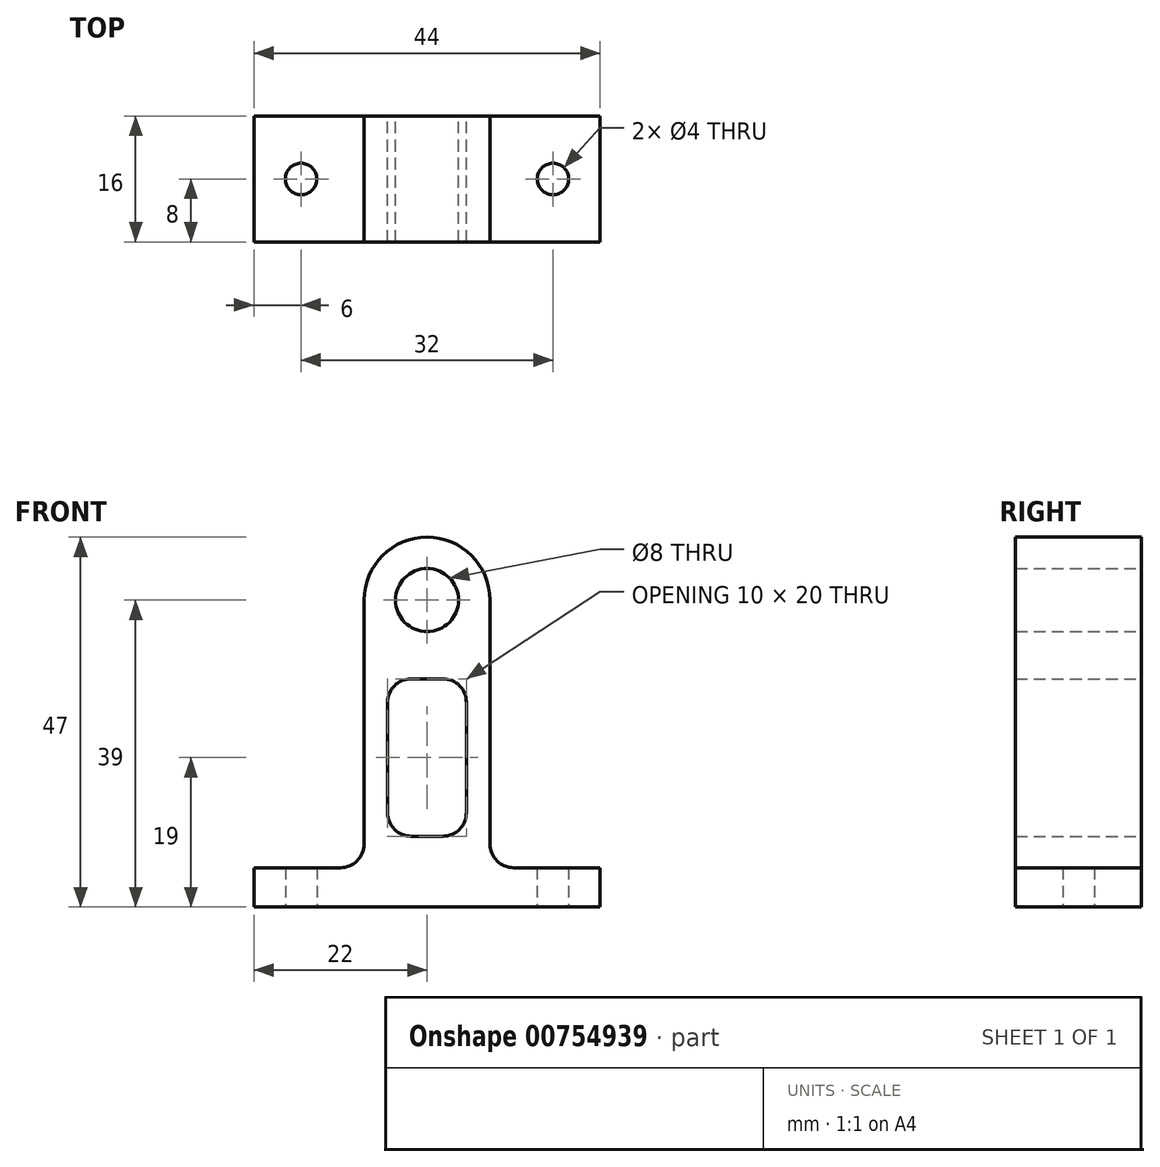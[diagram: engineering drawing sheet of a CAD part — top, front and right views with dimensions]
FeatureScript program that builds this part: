
annotation { "Feature Type Name" : "Feature", "Feature Type Description" : "" }
export const myFeature = defineFeature(function(context is Context, id is Id, definition is map)
    precondition{}
    {
        {
            var Q0;
            Q0=qCreatedBy(makeId("Front.planeOp"),FACE);
            var sketch = newSketch(context, id + "F0", { "sketchPlane" : qUnion([Q0])});
            skLineSegment(sketch, "E0.bottom", {"start": v(-22, 2.5) * mm, "end": v(-8, 2.5) * mm});
            skLineSegment(sketch, "E0.top", {"start": v(-22, -2.5) * mm, "end": v(22, -2.5) * mm});
            skLineSegment(sketch, "E0.left", {"start": v(-22, 2.5) * mm, "end": v(-22, -2.5) * mm});
            skLineSegment(sketch, "E0.right", {"start": v(22, 2.5) * mm, "end": v(22, -2.5) * mm});
            skPoint(sketch, "E0.middle", {"position": v(0, 0) * mm});
            skPoint(sketch, "E1", {"position": v(0, 36.5) * mm});
            skArc(sketch, "E2", {"start": v(8, 36.5) * mm, "mid": v(0, 44.5) * mm, "end": v(-8, 36.5) * mm});
            skLineSegment(sketch, "E3", {"start": v(8, 36.5) * mm, "end": v(8, 2.5) * mm});
            skLineSegment(sketch, "E4.0", {"start": v(-8, 36.5) * mm, "end": v(-8, 2.5) * mm});
            skLineSegment(sketch, "E5.trimOffspring", {"start": v(8, 2.5) * mm, "end": v(22, 2.5) * mm});
            skLineSegment(sketch, "E6.0", {"start": v(5, 26.5) * mm, "end": v(5, 6.5) * mm});
            skLineSegment(sketch, "E7.0", {"start": v(-5, 26.5) * mm, "end": v(-5, 6.5) * mm});
            skLineSegment(sketch, "E8.0", {"start": v(-5, 6.5) * mm, "end": v(5, 6.5) * mm});
            skLineSegment(sketch, "E9.0", {"start": v(-5, 26.5) * mm, "end": v(5, 26.5) * mm});
            skSolve(sketch);
        }
        {
            var Q0;
            Q0=makeQuery(id+"F0.imprint","IMPRINT",FACE,{"disambiguationData":[TD([[makeQuery(id+"F0.imprint","IMPRINT",EDGE,{"derivedFrom":sQuery(id+"F0.wireOp",EDGE,"E0.bottom")}),-1.0]])]});
            extrude(context, id + "F1", {"entities" : qUnion([Q0]), "depth" : 16 * mm, "offsetDistance" : 25 * mm});
        }
        {
            var Q0;
            Q0=sQuery(id+"F0.wireOp",VERTEX,"E1");
            var Q1;
            Q1=makeQuery(id+"F1.opExtrude","SWEPT_BODY",BODY,{"disambiguationData":[OSD([sQuery(id+"F0.wireOp",EDGE,"E0.bottom"),sQuery(id+"F0.wireOp",EDGE,"E0.top"),sQuery(id+"F0.wireOp",EDGE,"E0.left"),sQuery(id+"F0.wireOp",EDGE,"E0.right"),sQuery(id+"F0.wireOp",EDGE,"E2"),sQuery(id+"F0.wireOp",EDGE,"E3"),sQuery(id+"F0.wireOp",EDGE,"E4.0"),sQuery(id+"F0.wireOp",EDGE,"E5.trimOffspring")])]});
            hole(context, id + "F2", {"style" : HoleStyle.SIMPLE, "endStyle" : HoleEndStyle.THROUGH, "oppositeDirection" : true, "holeDiameter" : 8 * mm, "majorDiameter" : 5 * mm, "isTappedThrough" : true, "tappedDepth" : 8 * mm, "tapClearance" : 3, "locations" : qUnion([Q0]), "scope" : qUnion([Q1])});
        }
        {
            var Q0;
            Q0=makeQuery(id+"F1.opExtrude","SWEPT_FACE",FACE,{"disambiguationData":[OSD([sQuery(id+"F0.wireOp",EDGE,"E0.top")])]});
            var sketch = newSketch(context, id + "F3", { "sketchPlane" : qUnion([Q0])});
            skLineSegment(sketch, "E10.bottom", {"start": v(-22, 0) * mm, "end": v(22, 0) * mm});
            skLineSegment(sketch, "E10.top", {"start": v(-22, 16) * mm, "end": v(22, 16) * mm});
            skLineSegment(sketch, "E10.left", {"start": v(-22, 0) * mm, "end": v(-22, 16) * mm});
            skLineSegment(sketch, "E10.right", {"start": v(22, 0) * mm, "end": v(22, 16) * mm});
            skLineSegment(sketch, "E11.0", {"start": v(-16, 0) * mm, "end": v(-16, 16) * mm});
            skLineSegment(sketch, "E12.0", {"start": v(16, 0) * mm, "end": v(16, 16) * mm});
            skLineSegment(sketch, "E13.0", {"start": v(-18, 8) * mm, "end": v(22, 8) * mm});
            skPoint(sketch, "E14", {"position": v(-16, 8) * mm});
            skPoint(sketch, "E15", {"position": v(16, 8) * mm});
            skSolve(sketch);
        }
        {
            var Q0;
            Q0=sQuery(id+"F3.wireOp",VERTEX,"E14");
            var Q1;
            Q1=sQuery(id+"F3.wireOp",VERTEX,"E15");
            var Q2;
            Q2=makeQuery(id+"F1.opExtrude","SWEPT_BODY",BODY,{"disambiguationData":[OSD([sQuery(id+"F0.wireOp",EDGE,"E0.bottom"),sQuery(id+"F0.wireOp",EDGE,"E0.top"),sQuery(id+"F0.wireOp",EDGE,"E0.left"),sQuery(id+"F0.wireOp",EDGE,"E0.right"),sQuery(id+"F0.wireOp",EDGE,"E2"),sQuery(id+"F0.wireOp",EDGE,"E3"),sQuery(id+"F0.wireOp",EDGE,"E4.0"),sQuery(id+"F0.wireOp",EDGE,"E5.trimOffspring")])]});
            hole(context, id + "F4", {"style" : HoleStyle.SIMPLE, "endStyle" : HoleEndStyle.THROUGH, "holeDiameter" : 4 * mm, "majorDiameter" : 5 * mm, "isTappedThrough" : true, "tappedDepth" : 8 * mm, "tapClearance" : 3, "locations" : qUnion([Q0, Q1]), "scope" : qUnion([Q2])});
        }
        {
            var Q0;
            Q0=makeQuery(id+"F1.opExtrude","SWEPT_EDGE",EDGE,{"disambiguationData":[OSD([sQuery(id+"F0.wireOp",EDGE,"E0.bottom"),sQuery(id+"F0.wireOp",EDGE,"E4.0")])]});
            var Q1;
            Q1=makeQuery(id+"F1.opExtrude","SWEPT_EDGE",EDGE,{"disambiguationData":[OSD([sQuery(id+"F0.wireOp",EDGE,"E3"),sQuery(id+"F0.wireOp",EDGE,"E5.trimOffspring")])]});
            var Q2;
            Q2=makeQuery(id+"F1.opExtrude","SWEPT_EDGE",EDGE,{"disambiguationData":[OSD([sQuery(id+"F0.wireOp",EDGE,"E6.0"),sQuery(id+"F0.wireOp",EDGE,"E8.0")])]});
            var Q3;
            Q3=makeQuery(id+"F1.opExtrude","SWEPT_EDGE",EDGE,{"disambiguationData":[OSD([sQuery(id+"F0.wireOp",EDGE,"E7.0"),sQuery(id+"F0.wireOp",EDGE,"E8.0")])]});
            var Q4;
            Q4=makeQuery(id+"F1.opExtrude","SWEPT_EDGE",EDGE,{"disambiguationData":[OSD([sQuery(id+"F0.wireOp",EDGE,"E7.0"),sQuery(id+"F0.wireOp",EDGE,"E9.0")])]});
            var Q5;
            Q5=makeQuery(id+"F1.opExtrude","SWEPT_EDGE",EDGE,{"disambiguationData":[OSD([sQuery(id+"F0.wireOp",EDGE,"E6.0"),sQuery(id+"F0.wireOp",EDGE,"E9.0")])]});
            fillet(context, id + "F5", {"entities" : qUnion([Q0, Q1, Q2, Q3, Q4, Q5]), "radius" : 3 * mm, "tangentPropagation" : true, "allowEdgeOverflow" : false});
        }
    });
